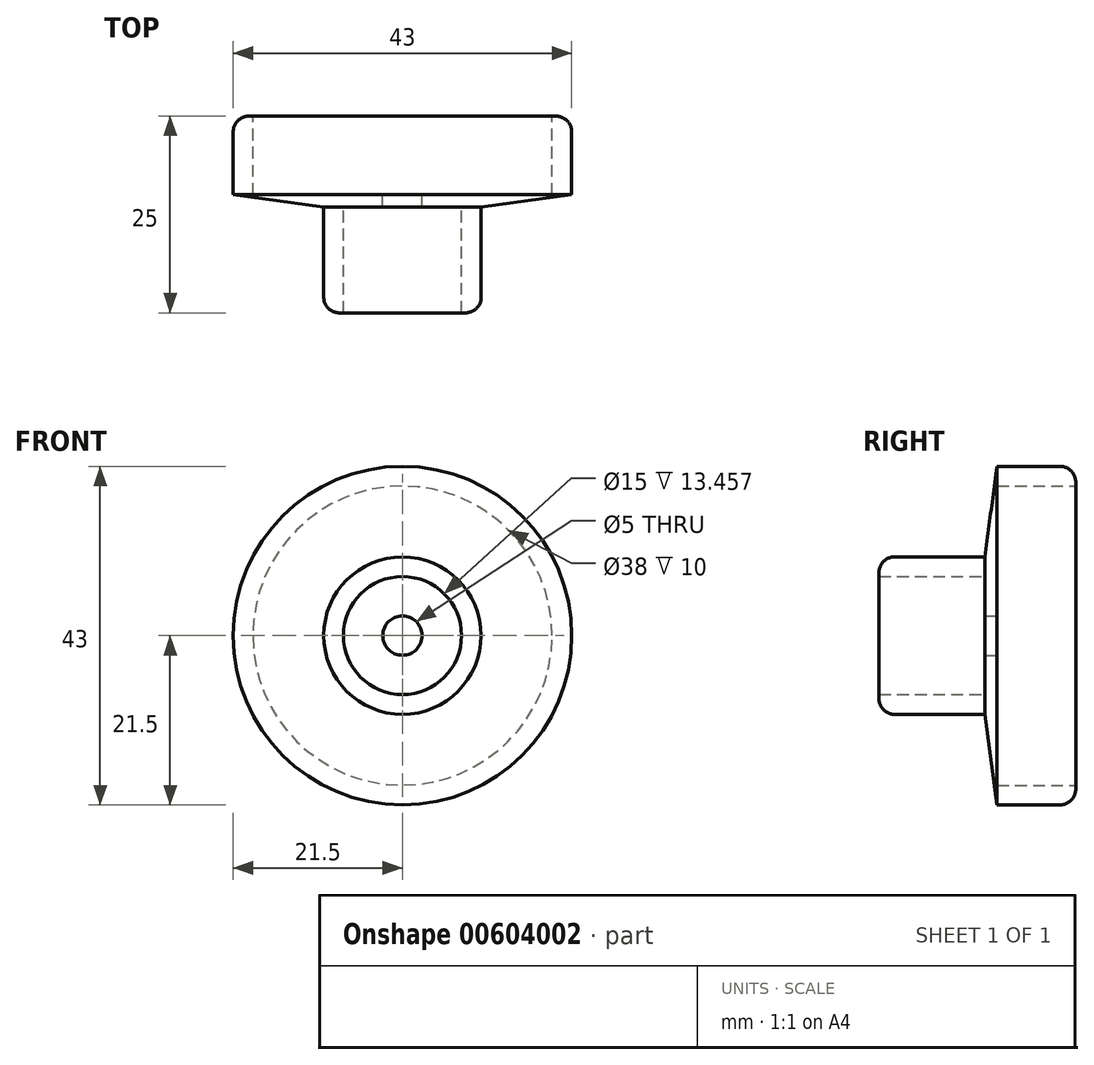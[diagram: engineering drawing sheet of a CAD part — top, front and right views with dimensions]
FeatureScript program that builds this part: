
annotation { "Feature Type Name" : "Feature", "Feature Type Description" : "" }
export const myFeature = defineFeature(function(context is Context, id is Id, definition is map)
    precondition{}
    {
        {
            var Q0;
            Q0=qCreatedBy(makeId("Front.planeOp"),FACE);
            var sketch = newSketch(context, id + "F0", { "sketchPlane" : qUnion([Q0])});
            skCircle(sketch, "E0", {"center": v(0, 0) * mm, "radius": 21.5 * mm});
            skCircle(sketch, "E1", {"center": v(0, 0) * mm, "radius": 19 * mm});
            skSolve(sketch);
        }
        {
            var Q0;
            Q0 = qSketchRegion(id + "F0", true);
            extrude(context, id + "F1", {"entities" : qUnion([Q0]), "depth" : 10 * mm, "offsetDistance" : 25.4 * mm});
        }
        {
            var Q0;
            Q0=makeQuery(id+"F1.opExtrude","CAP_FACE",FACE,{"disambiguationData":[OSD([sQuery(id+"F0.wireOp",EDGE,"E0")])],"isStart":false});
            cPlane(context, id + "F2", {"entities" : qUnion([Q0]), "cplaneType" : CPlaneType.OFFSET, "offset" : 0 * mm, "width" : 152.4 * mm, "height" : 152.4 * mm});
        }
        {
            var Q0;
            Q0=qCreatedBy(makeId("Right.planeOp"),FACE);
            var sketch = newSketch(context, id + "F3", { "sketchPlane" : qUnion([Q0])});
            skLineSegment(sketch, "E2", {"start": v(-10, 0) * mm, "end": v(-10, 21.5) * mm});
            skLineSegment(sketch, "E3", {"start": v(-10, 21.5) * mm, "end": v(-11.54, 10) * mm});
            skLineSegment(sketch, "E4", {"start": v(-11.54, 10) * mm, "end": v(-11.54, 0) * mm});
            skLineSegment(sketch, "E5", {"start": v(-11.54, 0) * mm, "end": v(-10, 0) * mm});
            skSolve(sketch);
        }
        {
            var Q0;
            Q0 = qSketchRegion(id + "F3", true);
            var Q1;
            Q1=sQuery(id+"F3.wireOp",EDGE,"E5");
            revolve(context, id + "F4", {"entities" : qUnion([Q0]), "axis" : qUnion([Q1]), "revolveType" : RevolveType.FULL});
        }
        {
            var Q0;
            Q0=qCreatedBy(id+"F2.planeOp",FACE);
            var sketch = newSketch(context, id + "F5", { "sketchPlane" : qUnion([Q0])});
            skCircle(sketch, "E6", {"center": v(0, 0) * mm, "radius": 10 * mm});
            skCircle(sketch, "E7", {"center": v(0, 0) * mm, "radius": 7.5 * mm});
            skSolve(sketch);
        }
        {
            var Q0;
            Q0 = qSketchRegion(id + "F5", true);
            extrude(context, id + "F6", {"entities" : qUnion([Q0]), "operationType" : NewBodyOperationType.ADD, "depth" : 15 * mm, "offsetDistance" : 25.4 * mm});
        }
        {
            var Q0;
            Q0=makeQuery(id+"F0.imprint","IMPRINT",FACE,{"disambiguationData":[TD([[makeQuery(id+"F0.imprint","IMPRINT",EDGE,{"derivedFrom":sQuery(id+"F0.wireOp",EDGE,"E1")}),1.0]])]});
            var sketch = newSketch(context, id + "F7", { "sketchPlane" : qUnion([Q0])});
            skCircle(sketch, "E8", {"center": v(0, 0) * mm, "radius": 5 * mm});
            skSolve(sketch);
        }
        {
            var Q0;
            Q0=sQuery(id+"F7.wireOp",VERTEX,"E8.center");
            var Q1;
            Q1=makeQuery(id+"F4.opRevolve","SWEPT_BODY",BODY,{"disambiguationData":[OSD([sQuery(id+"F3.wireOp",EDGE,"E2"),sQuery(id+"F3.wireOp",EDGE,"E3"),sQuery(id+"F3.wireOp",EDGE,"E4"),sQuery(id+"F3.wireOp",EDGE,"E5")])]});
            hole(context, id + "F8", {"style" : HoleStyle.SIMPLE, "endStyle" : HoleEndStyle.BLIND, "oppositeDirection" : true, "holeDiameter" : 5 * mm, "majorDiameter" : 6.35 * mm, "holeDepth" : 50.8 * mm, "isTappedThrough" : true, "tappedDepth" : 12.7 * mm, "tapClearance" : 3, "locations" : qUnion([Q0]), "scope" : qUnion([Q1])});
        }
        {
            var Q0;
            Q0=makeQuery(id+"F1.opExtrude","CAP_EDGE",EDGE,{"disambiguationData":[OSD([sQuery(id+"F0.wireOp",EDGE,"E0")])],"isStart":true});
            fillet(context, id + "F9", {"entities" : qUnion([Q0]), "radius" : 2 * mm, "tangentPropagation" : true, "allowEdgeOverflow" : false});
        }
        {
            var Q0;
            Q0=makeQuery(id+"F6.opExtrude","CAP_EDGE",EDGE,{"disambiguationData":[OSD([sQuery(id+"F5.wireOp",EDGE,"E6")])],"isStart":false});
            fillet(context, id + "F10", {"entities" : qUnion([Q0]), "radius" : 2 * mm, "tangentPropagation" : true, "allowEdgeOverflow" : false});
        }
    });
